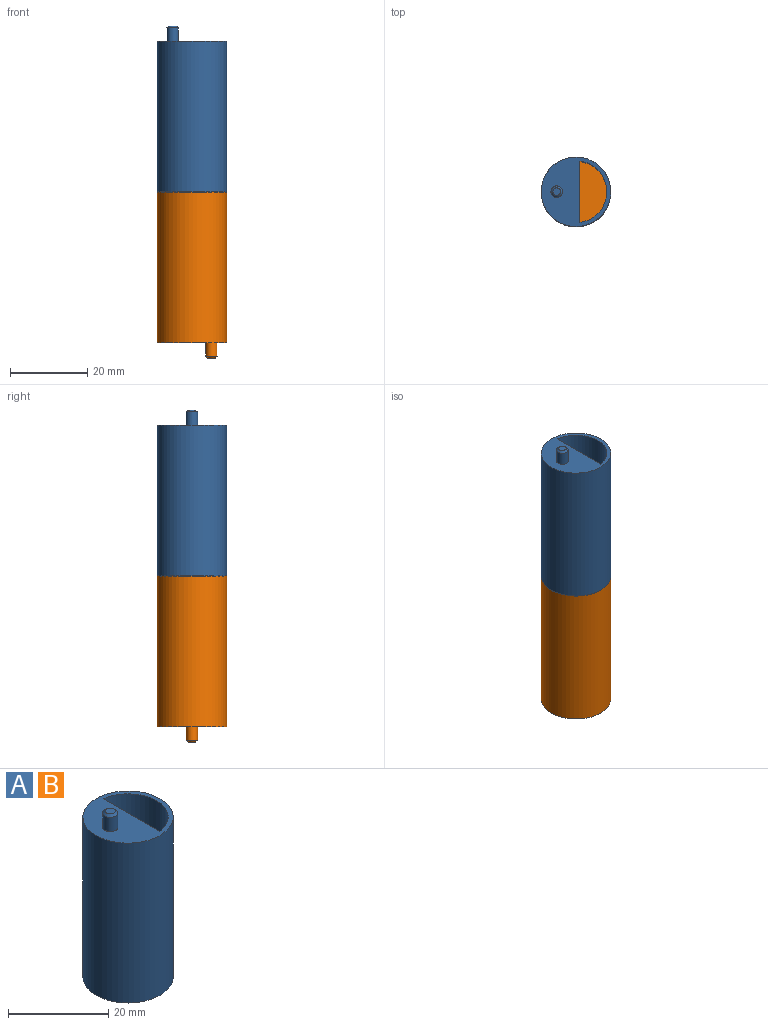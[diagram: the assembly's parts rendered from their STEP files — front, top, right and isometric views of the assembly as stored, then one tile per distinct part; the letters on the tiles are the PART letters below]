
ASSEMBLY  parts=2 mates=1
PART A: 11 faces, bbox 18x18x43 mm
  f0: cylinder r=8mm len=39mm, axis (0,0,1), area 902mm2, adj f2,f6,f8
  f1: cylinder r=9mm len=39mm, axis (0,0,-1), area 2205.4mm2, adj f2,f8
  f2: plane 18x18mm, normal (0,0,1), area 162.8mm2, adj f0,f1,f3,f6
  f3: cylinder r=1.5mm len=3.5mm, axis (0,0,-1), area 33mm2, adj f2,f10
  f4: plane 2x2mm, normal (0,0,1), area 3.1mm2, adj f10
  f5: cylinder r=8mm len=35.5mm, axis (0,0,1), area 821mm2, adj f7,f8,f9
  f6: plane 39x15.87mm, normal (1,0,0), area 619.1mm2, adj f0,f2,f8
  f7: plane 35.5x15.87mm, normal (-1,0,0), area 563.5mm2, adj f5,f8,f9
  f8: plane 18x18mm, normal (0,0,-1), area 85.3mm2, adj f0,f1,f5,f6,f7
  f9: plane 15.87x7mm, normal (0,0,-1), area 84.6mm2, adj f5,f7
  f10: cone r=1mm half-angle=45deg, axis (0,0,-1), area 5.6mm2, adj f3,f4
PART B: same geometry as A
PLACE A rot(axis=(0,-1,0),0deg) t=(-2.77,-4.51,7.36)mm
PLACE B rot(axis=(0,1,0),180deg) t=(-2.77,-4.51,-63.64)mm
MATE fastened A.f1 <-> B.f1  axis (0,0,-1) through (-2.77,-4.51,-28.14)mm
